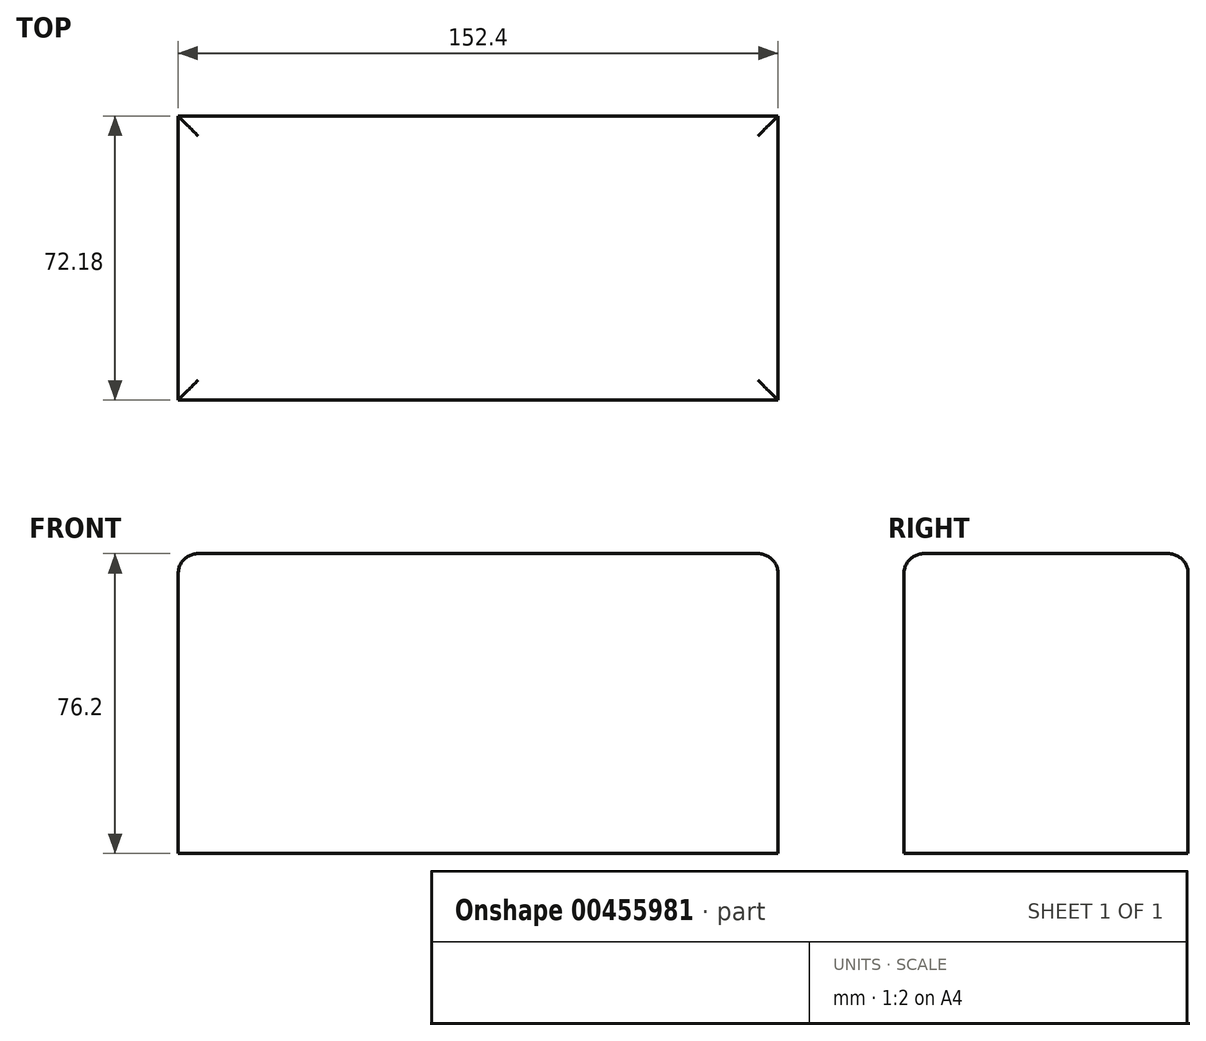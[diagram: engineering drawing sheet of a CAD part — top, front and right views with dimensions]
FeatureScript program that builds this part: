
annotation { "Feature Type Name" : "Feature", "Feature Type Description" : "" }
export const myFeature = defineFeature(function(context is Context, id is Id, definition is map)
    precondition{}
    {
        {
            var Q0;
            Q0=qCreatedBy(makeId("Top.planeOp"),FACE);
            var sketch = newSketch(context, id + "F0", { "sketchPlane" : qUnion([Q0])});
            skLineSegment(sketch, "E0.bottom", {"start": v(-76.2, 23.4) * mm, "end": v(76.2, 23.4) * mm});
            skLineSegment(sketch, "E0.top", {"start": v(-76.2, -23.4) * mm, "end": v(76.2, -23.4) * mm});
            skLineSegment(sketch, "E0.left", {"start": v(-76.2, 23.4) * mm, "end": v(-76.2, -23.4) * mm});
            skLineSegment(sketch, "E0.right", {"start": v(76.2, 23.4) * mm, "end": v(76.2, -23.4) * mm});
            skPoint(sketch, "E0.middle", {"position": v(0, 0) * mm});
            skSolve(sketch);
        }
        {
            var Q0;
            Q0=makeQuery(id+"F0.imprint","IMPRINT",FACE,{"disambiguationData":[TD([[makeQuery(id+"F0.imprint","IMPRINT",EDGE,{"derivedFrom":sQuery(id+"F0.wireOp",EDGE,"E0.bottom")}),-1.0]])]});
            extrude(context, id + "F1", {"entities" : qUnion([Q0]), "depth" : 76.2 * mm});
        }
        {
            var Q0;
            Q0=makeQuery(id+"F1.opExtrude","SWEPT_FACE",FACE,{"disambiguationData":[OSD([sQuery(id+"F0.wireOp",EDGE,"E0.top")])]});
            var sketch = newSketch(context, id + "F2", { "sketchPlane" : qUnion([Q0])});
            skSolve(sketch);
        }
        {
            var Q0;
            {var subQ0=sQuery(id+"F0.wireOp",EDGE,"E0.top");Q0=makeQuery(id+"F2.imprint","IMPRINT",FACE,{"disambiguationData":[TD([[makeQuery(id+"F2.imprint","IMPRINT",EDGE,{"derivedFrom":makeQuery(id+"F1.opExtrude","CAP_EDGE",EDGE,{"disambiguationData":[OSD([subQ0])],"isStart":true})}),1.0]])]});}
            extrude(context, id + "F3", {"entities" : qUnion([Q0]), "operationType" : NewBodyOperationType.ADD, "depth" : 25.4 * mm});
        }
        {
            var Q0;
            {var subQ0=sQuery(id+"F0.wireOp",EDGE,"E0.top");Q0=makeQuery(id+"F3.boolean.opBoolean","MERGE",FACE,{"derivedFrom":[makeQuery(id+"F1.opExtrude","CAP_FACE",FACE,{"disambiguationData":[OSD([sQuery(id+"F0.wireOp",EDGE,"E0.bottom"),subQ0,sQuery(id+"F0.wireOp",EDGE,"E0.left"),sQuery(id+"F0.wireOp",EDGE,"E0.right")])],"isStart":false}),makeQuery(id+"F3.opExtrude","SWEPT_FACE",FACE,{"disambiguationData":[OSD([subQ0]),TDD([makeQuery(id+"F2.imprint","IMPRINT",EDGE,{"derivedFrom":makeQuery(id+"F1.opExtrude","CAP_EDGE",EDGE,{"disambiguationData":[OSD([subQ0])],"isStart":false})})])]})]});}
            var Q1;
            {var subQ0=sQuery(id+"F0.wireOp",EDGE,"E0.top");Q1=makeQuery(id+"F3.opExtrude","CAP_EDGE",EDGE,{"disambiguationData":[OSD([subQ0]),TDD([makeQuery(id+"F2.imprint","IMPRINT",EDGE,{"derivedFrom":makeQuery(id+"F1.opExtrude","CAP_EDGE",EDGE,{"disambiguationData":[OSD([subQ0])],"isStart":false})})])],"isStart":false});}
            fillet(context, id + "F4", {"entities" : qUnion([Q0, Q1]), "radius" : 5.08 * mm, "tangentPropagation" : true, "allowEdgeOverflow" : false});
        }
    });
